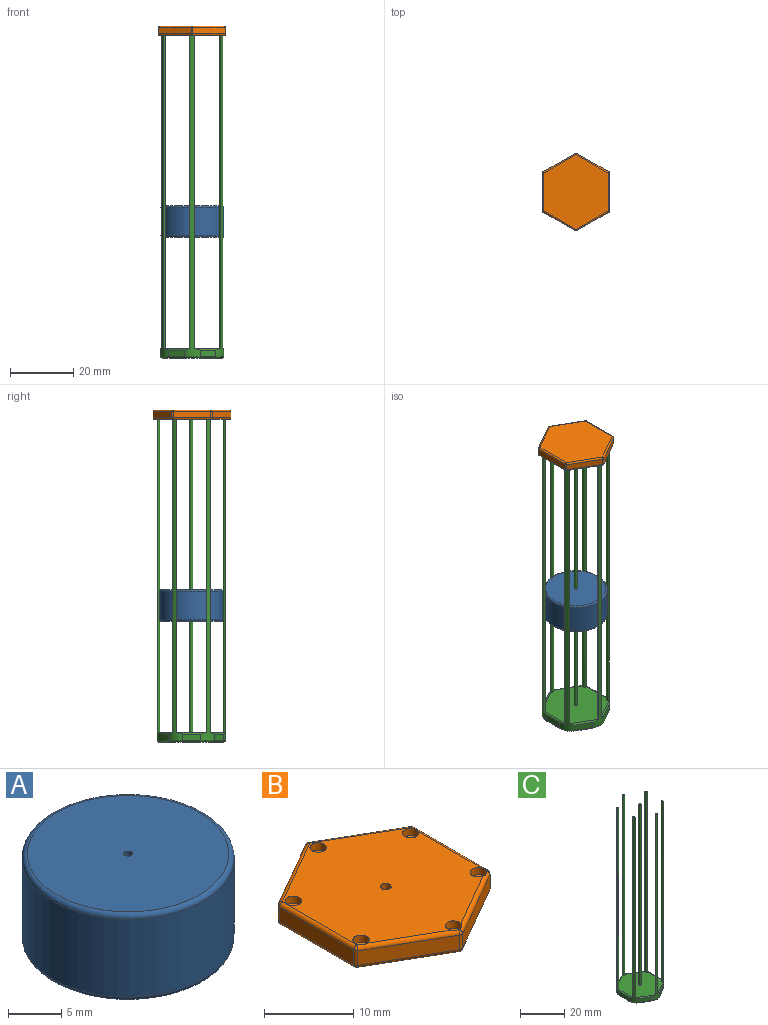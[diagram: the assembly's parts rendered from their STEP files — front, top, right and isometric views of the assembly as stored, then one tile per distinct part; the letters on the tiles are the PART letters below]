
ASSEMBLY  parts=3 mates=2
PART A: 6 faces, bbox 21.6x21.6x10 mm
  f0: cylinder r=0.4mm len=10mm, axis (0,0,-1), area 25.1mm2, adj f2,f3
  f1: cylinder r=10mm len=20mm, axis (0,0,-1), area 565.5mm2, adj f4,f5
  f2: plane 19x19mm, normal (0,0,1), area 283mm2, adj f0,f5
  f3: plane 19x19mm, normal (0,0,-1), area 283mm2, adj f0,f4
  f4: torus R=9.5mm, axis (0,0,1), area 48.5mm2, adj f1,f3
  f5: torus R=9.5mm, axis (0,0,1), area 48.5mm2, adj f1,f2
PART B: 52 faces, bbox 21.4x24.6x3 mm
  f0: plane 10.22x5.9mm, normal (-0.5,0.87,0), area 23.6mm2, adj f24,f28,f30,f46
  f1: plane 11.8x2mm, normal (-1,0,0), area 23.6mm2, adj f22,f30,f32,f50
  f2: plane 10.22x5.9mm, normal (-0.5,-0.87,0), area 23.6mm2, adj f23,f32,f34,f49
  f3: plane 10.22x5.9mm, normal (0.5,-0.87,0), area 23.6mm2, adj f25,f34,f36,f45
  f4: plane 11.8x2mm, normal (1,0,0), area 23.6mm2, adj f27,f36,f38,f41
  f5: plane 10.22x5.9mm, normal (0.5,0.87,0), area 23.6mm2, adj f26,f28,f38,f42
  f6: plane 23.18x20.44mm, normal (0,0,1), area 345.4mm2, adj f8,f10,f12,f14,f16,f18,f20,f22
  f7: plane 23.6x20.44mm, normal (0,0,-1), area 361.8mm2, adj f41,f42,f45,f46,f49,f50
  f8: cylinder r=0.92mm len=1.84mm, axis (0,0,1), area 5.8mm2, adj f6,f9
  f9: plane 1.84x1.84mm, normal (0,0,1), area 2.7mm2, adj f8
  f10: cylinder r=0.92mm len=1.84mm, axis (0,0,1), area 5.8mm2, adj f6,f11,f23
  f11: plane 1.84x1.84mm, normal (0,0,1), area 2.7mm2, adj f10
  f12: cylinder r=0.92mm len=1.84mm, axis (0,0,1), area 5.7mm2, adj f6,f13,f23,f25,f35
  f13: plane 1.84x1.84mm, normal (0,0,1), area 2.7mm2, adj f12
  f14: cylinder r=0.92mm len=1.84mm, axis (0,0,1), area 5.7mm2, adj f6,f15,f25,f27,f37
  f15: plane 1.84x1.84mm, normal (0,0,1), area 2.7mm2, adj f14
  f16: cylinder r=0.92mm len=1.84mm, axis (0,0,1), area 5.8mm2, adj f6,f17,f27
  f17: plane 1.84x1.84mm, normal (0,0,1), area 2.7mm2, adj f16
  f18: cylinder r=0.92mm len=1.84mm, axis (0,0,1), area 5.8mm2, adj f6,f19
  f19: plane 1.84x1.84mm, normal (0,0,1), area 2.7mm2, adj f18
  f20: cylinder r=0.6mm len=1.2mm, axis (0,0,1), area 3.8mm2, adj f6,f21
  f21: plane 1.2x1.2mm, normal (0,0,1), area 1.1mm2, adj f20
  f22: cylinder r=0.5mm len=11.8mm, axis (0,1,0), area 9.3mm2, adj f1,f6,f31,f33
  f23: cylinder r=0.5mm len=10.47mm, axis (-0.87,0.5,0), area 9.1mm2, adj f2,f6,f10,f12,f33,f35
  f24: cylinder r=0.5mm len=10.47mm, axis (0.87,0.5,0), area 9.3mm2, adj f0,f6,f29,f31
  f25: cylinder r=0.5mm len=10.47mm, axis (-0.87,-0.5,0), area 8.9mm2, adj f3,f6,f12,f14,f35,f37
  f26: cylinder r=0.5mm len=10.47mm, axis (0.87,-0.5,0), area 9.3mm2, adj f5,f6,f29,f39
  f27: cylinder r=0.5mm len=11.8mm, axis (0,-1,0), area 9.2mm2, adj f4,f6,f14,f16,f37,f39
  f28: cylinder r=0.5mm len=2mm, axis (0,0,-1), area 1mm2, adj f0,f5,f29,f44
  f29: sphere r=0.5mm, area 0.5mm2, adj f24,f26,f28
  f30: cylinder r=0.5mm len=2mm, axis (0,0,-1), area 1mm2, adj f0,f1,f31,f48
  f31: sphere r=0.5mm, area 0.3mm2, adj f22,f24,f30
  f32: cylinder r=0.5mm len=2mm, axis (0,0,-1), area 1mm2, adj f1,f2,f33,f51
  f33: sphere r=0.5mm, area 0.3mm2, adj f22,f23,f32
  f34: cylinder r=0.5mm len=2mm, axis (0,0,-1), area 1mm2, adj f2,f3,f35,f47
  f35: sphere r=0.5mm, area 0.3mm2, adj f12,f23,f25,f34
  f36: cylinder r=0.5mm len=2mm, axis (0,0,-1), area 1mm2, adj f3,f4,f37,f43
  f37: sphere r=0.5mm, area 0.3mm2, adj f14,f25,f27,f36
  f38: cylinder r=0.5mm len=2mm, axis (0,0,-1), area 1mm2, adj f4,f5,f39,f40
  f39: sphere r=0.5mm, area 0.2mm2, adj f26,f27,f38
  f40: sphere r=0.5mm, area 0.2mm2, adj f38,f41,f42
  f41: cylinder r=0.5mm len=11.8mm, axis (0,1,0), area 9.3mm2, adj f4,f7,f40,f43
  f42: cylinder r=0.5mm len=10.47mm, axis (-0.87,0.5,0), area 9.3mm2, adj f5,f7,f40,f44
  f43: sphere r=0.5mm, area 0.3mm2, adj f36,f41,f45
  f44: sphere r=0.5mm, area 0.5mm2, adj f28,f42,f46
  f45: cylinder r=0.5mm len=10.47mm, axis (0.87,0.5,0), area 9.3mm2, adj f3,f7,f43,f47
  f46: cylinder r=0.5mm len=10.47mm, axis (-0.87,-0.5,0), area 9.3mm2, adj f0,f7,f44,f48
  f47: sphere r=0.5mm, area 0.3mm2, adj f34,f45,f49
  f48: sphere r=0.5mm, area 0.3mm2, adj f30,f46,f50
  f49: cylinder r=0.5mm len=10.47mm, axis (0.87,-0.5,0), area 9.3mm2, adj f2,f7,f47,f51
  f50: cylinder r=0.5mm len=11.8mm, axis (0,-1,0), area 9.3mm2, adj f1,f7,f48,f51
  f51: sphere r=0.5mm, area 0.3mm2, adj f32,f49,f50
PART C: 46 faces, bbox 20.9x22.4x103 mm
  f0: plane 20.59x19.05mm, normal (0,0,-1), area 307.4mm2, adj f28,f29,f30,f31,f32,f33,f35,f37
  f1: plane 5.01x2.91mm, normal (-0.5,-0.86,0), area 11.6mm2, adj f25,f30,f40,f44
  f2: plane 5.03x2.89mm, normal (0.5,-0.87,0), area 11.6mm2, adj f24,f28,f42,f44
  f3: plane 5.8x2mm, normal (1,0,0), area 11.6mm2, adj f26,f29,f38,f42
  f4: plane 5.01x2.91mm, normal (0.5,0.86,0), area 11.6mm2, adj f22,f31,f36,f38
  f5: plane 5.03x2.89mm, normal (-0.5,0.87,0), area 11.6mm2, adj f23,f33,f34,f36
  f6: plane 5.8x2mm, normal (-1,0,0), area 11.6mm2, adj f27,f32,f34,f40
  f7: plane 21.2x19.06mm, normal (0,0,1), area 307.9mm2, adj f8,f10,f12,f14,f16,f18,f20,f22
  f8: cylinder r=0.72mm len=100.02mm, axis (0,0,-1), area 227mm2, adj f7,f9,f23,f27,f34
  f9: plane 1.35x1.08mm, normal (0,0,1), area 0.9mm2, adj f8,f34
  f10: cylinder r=0.72mm len=100.02mm, axis (0,0,-1), area 227mm2, adj f7,f11,f24,f26,f42
  f11: plane 1.35x1.08mm, normal (0,0,1), area 0.9mm2, adj f10,f42
  f12: cylinder r=0.72mm len=100.02mm, axis (0,0,-1), area 227mm2, adj f7,f13,f25,f27,f40
  f13: plane 1.34x1.09mm, normal (0,0,1), area 0.9mm2, adj f12,f40
  f14: cylinder r=0.72mm len=100.02mm, axis (0,0,-1), area 227mm2, adj f7,f15,f24,f25,f44
  f15: plane 1.44x0.78mm, normal (0,0,1), area 0.9mm2, adj f14,f44
  f16: cylinder r=0.72mm len=100.02mm, axis (0,0,-1), area 227mm2, adj f7,f17,f22,f23,f36
  f17: plane 1.44x0.78mm, normal (0,0,1), area 0.9mm2, adj f16,f36
  f18: cylinder r=0.72mm len=100.02mm, axis (0,0,-1), area 227mm2, adj f7,f19,f22,f26,f38
  f19: plane 1.34x1.09mm, normal (0,0,1), area 0.9mm2, adj f18,f38
  f20: cylinder r=0.5mm len=100mm, axis (0,0,-1), area 314.2mm2, adj f7,f21
  f21: plane 1x1mm, normal (0,0,1), area 0.8mm2, adj f20
  f22: cylinder r=0.5mm len=8.47mm, axis (0.86,-0.5,0), area 6.3mm2, adj f4,f7,f16,f18,f36,f38
  f23: cylinder r=0.5mm len=8.49mm, axis (0.87,0.5,0), area 6.3mm2, adj f5,f7,f8,f16,f34,f36
  f24: cylinder r=0.5mm len=8.49mm, axis (-0.87,-0.5,0), area 6.3mm2, adj f2,f7,f10,f14,f42,f44
  f25: cylinder r=0.5mm len=8.47mm, axis (-0.86,0.5,0), area 6.3mm2, adj f1,f7,f12,f14,f40,f44
  f26: cylinder r=0.5mm len=9.5mm, axis (0,-1,0), area 6.3mm2, adj f3,f7,f10,f18,f38,f42
  f27: cylinder r=0.5mm len=9.5mm, axis (0,1,0), area 6.3mm2, adj f6,f7,f8,f12,f34,f40
  f28: cylinder r=0.5mm len=5.28mm, axis (0.87,0.5,0), area 4.6mm2, adj f0,f2,f43,f45
  f29: cylinder r=0.5mm len=5.8mm, axis (0,1,0), area 4.6mm2, adj f0,f3,f39,f43
  f30: cylinder r=0.5mm len=5.26mm, axis (0.86,-0.5,0), area 4.6mm2, adj f0,f1,f41,f45
  f31: cylinder r=0.5mm len=5.26mm, axis (-0.86,0.5,0), area 4.6mm2, adj f0,f4,f37,f39
  f32: cylinder r=0.5mm len=5.8mm, axis (0,-1,0), area 4.6mm2, adj f0,f6,f35,f41
  f33: cylinder r=0.5mm len=5.28mm, axis (-0.87,-0.5,0), area 4.6mm2, adj f0,f5,f35,f37
  f34: cylinder r=5mm len=102.5mm, axis (0,0,-1), area 156.5mm2, adj f5,f6,f8,f9,f23,f27,f35
  f35: torus R=4.5mm, axis (0,0,1), area 4mm2, adj f0,f32,f33,f34
  f36: cylinder r=5mm len=102.5mm, axis (0,0,-1), area 156.5mm2, adj f4,f5,f16,f17,f22,f23,f37
  f37: torus R=4.5mm, axis (0,0,1), area 4mm2, adj f0,f31,f33,f36
  f38: cylinder r=5mm len=102.5mm, axis (0,0,-1), area 156.5mm2, adj f3,f4,f18,f19,f22,f26,f39
  f39: torus R=4.5mm, axis (0,0,1), area 4mm2, adj f0,f29,f31,f38
  f40: cylinder r=5mm len=102.5mm, axis (0,0,-1), area 156.5mm2, adj f1,f6,f12,f13,f25,f27,f41
  f41: torus R=4.5mm, axis (0,0,1), area 4mm2, adj f0,f30,f32,f40
  f42: cylinder r=5mm len=102.5mm, axis (0,0,-1), area 156.5mm2, adj f2,f3,f10,f11,f24,f26,f43
  f43: torus R=4.5mm, axis (0,0,1), area 4mm2, adj f0,f28,f29,f42
  f44: cylinder r=5mm len=102.5mm, axis (0,0,-1), area 156.5mm2, adj f1,f2,f14,f15,f24,f25,f45
  f45: torus R=4.5mm, axis (0,0,1), area 4mm2, adj f0,f28,f30,f44
PLACE A t=(-31.72,15.79,11.81)mm
PLACE B rot(axis=(1,0,0),180deg) t=(-31.8,15.58,78.69)mm
PLACE C t=(-31.72,15.79,-26.31)mm fixed
MATE fastened B.f20 <-> C.f20  axis (0,0,-1) through (-31.72,15.79,75.69)mm
MATE slider C.f20 <-> A.f0  axis (0,0,-1) through (-31.72,15.79,26.69)mm
